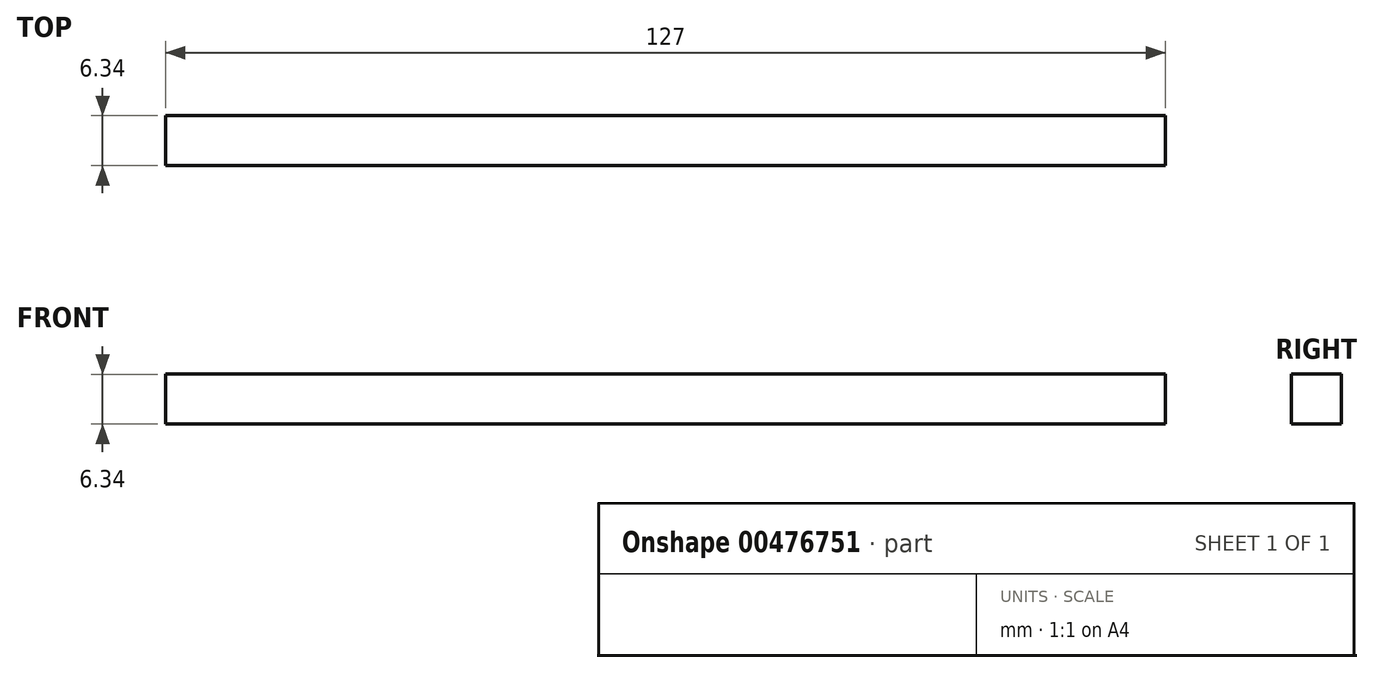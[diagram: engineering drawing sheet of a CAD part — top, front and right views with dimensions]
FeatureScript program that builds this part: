
annotation { "Feature Type Name" : "Feature", "Feature Type Description" : "" }
export const myFeature = defineFeature(function(context is Context, id is Id, definition is map)
    precondition{}
    {
        {
            var Q0;
            Q0=qCreatedBy(makeId("Front.planeOp"),FACE);
            var sketch = newSketch(context, id + "F0", { "sketchPlane" : qUnion([Q0])});
            skLineSegment(sketch, "E0.bottom", {"start": v(63.5, -3.17) * mm, "end": v(-63.5, -3.18) * mm});
            skLineSegment(sketch, "E0.top", {"start": v(63.5, 3.18) * mm, "end": v(-63.5, 3.17) * mm});
            skLineSegment(sketch, "E0.left", {"start": v(63.5, -3.17) * mm, "end": v(63.5, 3.18) * mm});
            skLineSegment(sketch, "E0.right", {"start": v(-63.5, -3.18) * mm, "end": v(-63.5, 3.17) * mm});
            skPoint(sketch, "E0.middle", {"position": v(0, 0) * mm});
            skSolve(sketch);
        }
        {
            var Q0;
            Q0 = qSketchRegion(id + "F0", true);
            extrude(context, id + "F1", {"entities" : qUnion([Q0]), "depth" : 6.35 * mm, "symmetric" : true});
        }
    });
